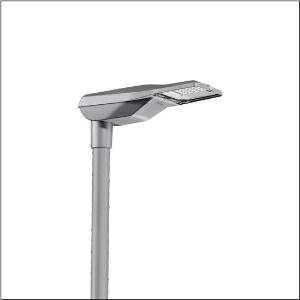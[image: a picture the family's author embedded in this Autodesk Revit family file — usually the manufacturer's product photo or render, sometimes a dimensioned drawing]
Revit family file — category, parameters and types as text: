
# Revit family: streetlight_sl_21_micro___st1_0a_5xe5d43a08cb_bbe5
name_source: partatom
category: Lighting Fixtures
units: mm (PartAtom-declared; Revit-internal decimal feet)

## family parameters
Cut with Voids When Loaded = No
Host = Face
Light Source = No
Part Type = Normal
Room Calculation Point = No
Round Connector Dimension = Use Diameter
Shared = No

## types (1)
- --- (1 x LED, 2380 lm, 15.8 W, 4000K)
    Apparent Load = 16 VA
    CIE Flux Codes = 37 72 97 100 100
    Color Rendering = 70
    Color Temperature = 4000K
    Default Elevation = 1800 mm
    Description = Streetlight SL 21 micro, mast luminaire, primary light control with lens, of PMMA, primary optical cover: cover, of toughened safety glass, transparent, light distribution: ST1.0a, light emission: direct distribution, primary light characteristic: asymmetric, installation type: side-entry, post-top, LED, 3G 1.5mm², High Power LED, rated luminous flux: 2.380lm, luminous efficacy: 151lm/W, light colour: 740, colour temperature: 4000K, control: flexible luminous flux parameterisation, time-dependent luminous flux control, constant luminous flux control, overheat protection, mains connection: 230..240V, AC, 50/60Hz, connection cable pre-assembled, cable length: 5,5m, wiring characteristics: H07RN-F, start of lifetime: 16W, end of service life: 16W, reduction: 9W, luminaire housing, of diecast aluminium, powder-coated, Siteco® metallic grey (DB 702S), corrosivity category C5 mid according to DIN EN ISO 12944, please order mast flange separately, inclination adjustable: 0°, 5°, 10°, 15°, sealing non-destructively replaceable, multi-level sealing system, length: 528mm, width: 235mm, height: 110mm, mast flange for spigot size: 42mm (side-entry): 5XC10008XM4, 60/48mm (side-entry/post-top): 5XC10108XM2, 76/60mm (side-entry/post-top): 5XC10108XM1, protection rating (complete): IP66, insulation class (complete): insulation class II (safety insulation), certification: CE, ENEC, ENEC+, VDE, impact resistance: IK09, permissible operating ambient temperature for outdoor applications: -40..+50°C, standard-compliant lighting for roads and squares, packaging unit: 1 piece

Light Distribution: ST1.0a
    Height = 110 mm
    Lamp = 1 x LED
    Lamp Light Flux = 2380 lm
    Lamp Power = 15.8 W
    Lamp count = 1
    Length = 528 mm
    Luminous efficacy = 151 lm/W
    Manufacturer = Siteco
    ModVariant = No
    Model = 5XE5D43A08CB
    Number of Poles = 1
    OnlyDefault = Yes
    Power Factor = 1
    Product Name = Streetlight SL 21 micro | ST1.0a
    Product group = mast luminaire | pylon top
    ProductGroupID = 6100
    Protection Class = Protection class II
    Protection Degree = IP 66
    RLX_Detail_Level = 1
    RLX_Emergency_Light_Flux = 0 lm
    RLX_Emergency_Type = 0
    RLX_Emergency_Type_DB = No
    RlxData = <blob elided: 98517 chars, md5=431ce126>
    Socket = socket
    Standby Power = 0 W
    System Light Flux = 2380 lm
    System Power = 16 W
    Type Comments = factory setting: luminous flux: 100 % | Output Level: 100 % | 300 mA
    Type Image = l_1006881.jpg
    URL = http://relux.com
    VarID = @adj_125973
    Voltage = 0 V
    Weight = 0.00 kg
    Width = 235 mm

## geometry (parser evidence)
native form markers: Blend x4, Sweep x10
no freeform markers — native parametric forms only
